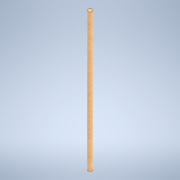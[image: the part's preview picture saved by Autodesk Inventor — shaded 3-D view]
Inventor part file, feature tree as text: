
AUTODESK INVENTOR PART (.ipt)
format: ipt  version: 2020.1 (Build 241239000, 239)  size: 93,696 bytes
history: native  units: mm
features: extrude x1, sketch x1
ambient origin geometry x8: Origin, YZ Plane, XZ Plane, XY Plane, X Axis, Y Axis, Z Axis, Center Point
bodies: Solid1 (feature_tree)
feature tree (2):
  extrude  "Extrusion1"  Depth=210.0mm TaperAngle=0.0deg
  sketch  "Sketch1"  dims[d0=6.35mm d1=210.0mm d2=0.0mm]
